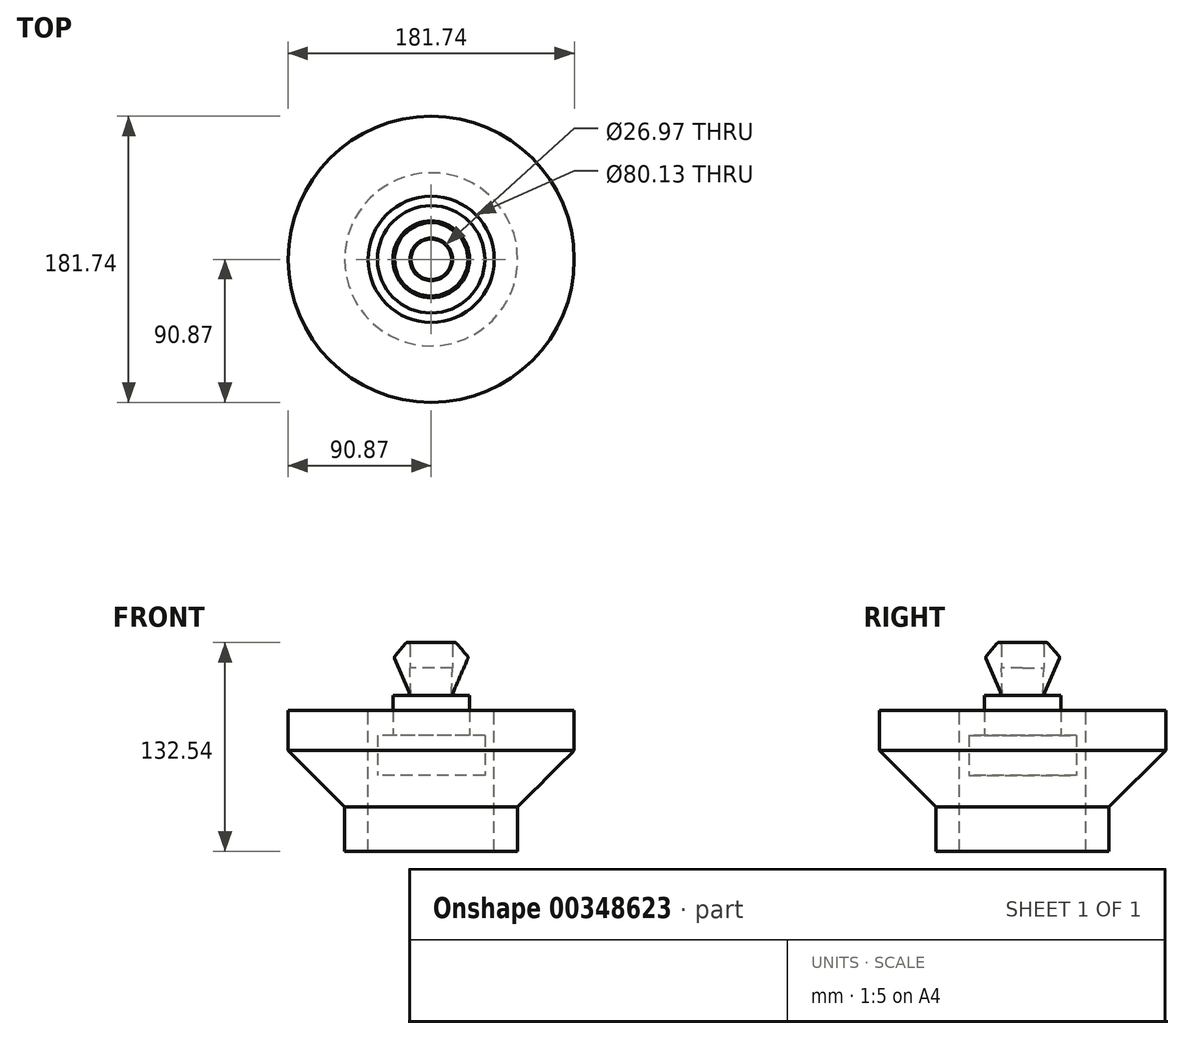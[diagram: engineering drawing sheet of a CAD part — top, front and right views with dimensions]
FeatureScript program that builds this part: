
annotation { "Feature Type Name" : "Feature", "Feature Type Description" : "" }
export const myFeature = defineFeature(function(context is Context, id is Id, definition is map)
    precondition{}
    {
        {
            var Q0;
            Q0=qCreatedBy(makeId("Top.planeOp"),FACE);
            var sketch = newSketch(context, id + "F0", { "sketchPlane" : qUnion([Q0])});
            skCircle(sketch, "E0", {"center": v(0, 0) * mm, "radius": 34.1 * mm});
            skSolve(sketch);
        }
        {
            var Q0;
            Q0 = qSketchRegion(id + "F0", true);
            extrude(context, id + "F1", {"entities" : qUnion([Q0]), "depth" : 25.4 * mm});
        }
        {
            var Q0;
            Q0=makeQuery(id+"F1.opExtrude","CAP_FACE",FACE,{"disambiguationData":[OSD([sQuery(id+"F0.wireOp",EDGE,"E0")])],"isStart":false});
            var sketch = newSketch(context, id + "F2", { "sketchPlane" : qUnion([Q0])});
            skCircle(sketch, "E1", {"center": v(0, 0) * mm, "radius": 24.36 * mm});
            skSolve(sketch);
        }
        {
            var Q0;
            Q0=makeQuery(id+"F2.imprint","IMPRINT",FACE,{"disambiguationData":[TD([[makeQuery(id+"F2.imprint","IMPRINT",EDGE,{"derivedFrom":sQuery(id+"F2.wireOp",EDGE,"E1")}),1.0]])]});
            extrude(context, id + "F3", {"entities" : qUnion([Q0]), "operationType" : NewBodyOperationType.ADD, "depth" : 25.4 * mm});
        }
        {
            var Q0;
            Q0=qCreatedBy(makeId("Right.planeOp"),FACE);
            var sketch = newSketch(context, id + "F4", { "sketchPlane" : qUnion([Q0])});
            skLineSegment(sketch, "E2", {"start": v(12.86, 50.2) * mm, "end": v(23.65, 74.9) * mm});
            skLineSegment(sketch, "E3", {"start": v(23.65, 74.9) * mm, "end": v(13.48, 86.92) * mm});
            skLineSegment(sketch, "E4", {"start": v(13.48, 86.92) * mm, "end": v(13.48, 68.05) * mm});
            skLineSegment(sketch, "E5", {"start": v(13.48, 68.05) * mm, "end": v(12.86, 50.2) * mm});
            skSolve(sketch);
        }
        {
            var Q0;
            Q0=makeQuery(id+"F4.imprint","IMPRINT",FACE,{"disambiguationData":[TD([[makeQuery(id+"F4.imprint","IMPRINT",EDGE,{"derivedFrom":sQuery(id+"F4.wireOp",EDGE,"E2")}),1.0]])]});
            var Q1;
            Q1=makeQuery(id+"F3.opExtrude","CAP_EDGE",EDGE,{"disambiguationData":[OSD([sQuery(id+"F2.wireOp",EDGE,"E1")])],"isStart":false});
            revolve(context, id + "F5", {"operationType" : NewBodyOperationType.ADD, "entities" : qUnion([Q0]), "axis" : qUnion([Q1]), "revolveType" : RevolveType.FULL});
        }
        {
            var Q0;
            Q0=makeQuery(id+"F5.opRevolve","SWEPT_FACE",FACE,{"disambiguationData":[OSD([sQuery(id+"F4.wireOp",EDGE,"E3")])]});
            var Q1;
            Q1=makeQuery(id+"F5.opRevolve","SWEPT_FACE",FACE,{"disambiguationData":[OSD([sQuery(id+"F4.wireOp",EDGE,"E2")])]});
            fillet(context, id + "F6", {"entities" : qUnion([Q0, Q1]), "radius" : 1.52 * mm, "tangentPropagation" : true, "allowEdgeOverflow" : false});
        }
        {
            var Q0;
            Q0=qCreatedBy(makeId("Front.planeOp"),FACE);
            var sketch = newSketch(context, id + "F7", { "sketchPlane" : qUnion([Q0])});
            skLineSegment(sketch, "E6", {"start": v(90.87, 15.84) * mm, "end": v(54.94, -20.08) * mm});
            skLineSegment(sketch, "E7", {"start": v(54.94, -20.08) * mm, "end": v(54.94, -48.26) * mm});
            skLineSegment(sketch, "E8", {"start": v(54.94, -48.26) * mm, "end": v(40.07, -48.23) * mm});
            skLineSegment(sketch, "E9", {"start": v(40.07, -48.23) * mm, "end": v(40.07, 41.24) * mm});
            skLineSegment(sketch, "E10", {"start": v(40.07, 41.24) * mm, "end": v(90.87, 41.24) * mm});
            skLineSegment(sketch, "E11", {"start": v(90.87, 41.24) * mm, "end": v(90.87, 15.84) * mm});
            skSolve(sketch);
        }
        {
            var Q0;
            Q0=makeQuery(id+"F7.imprint","IMPRINT",FACE,{"disambiguationData":[TD([[makeQuery(id+"F7.imprint","IMPRINT",EDGE,{"derivedFrom":sQuery(id+"F7.wireOp",EDGE,"E6")}),-1.0]])]});
            var Q1;
            Q1=makeQuery(id+"F1.opExtrude","SWEPT_FACE",FACE,{"disambiguationData":[OSD([sQuery(id+"F0.wireOp",EDGE,"E0")])]});
            revolve(context, id + "F8", {"entities" : qUnion([Q0]), "axis" : qUnion([Q1]), "revolveType" : RevolveType.FULL});
        }
    });
